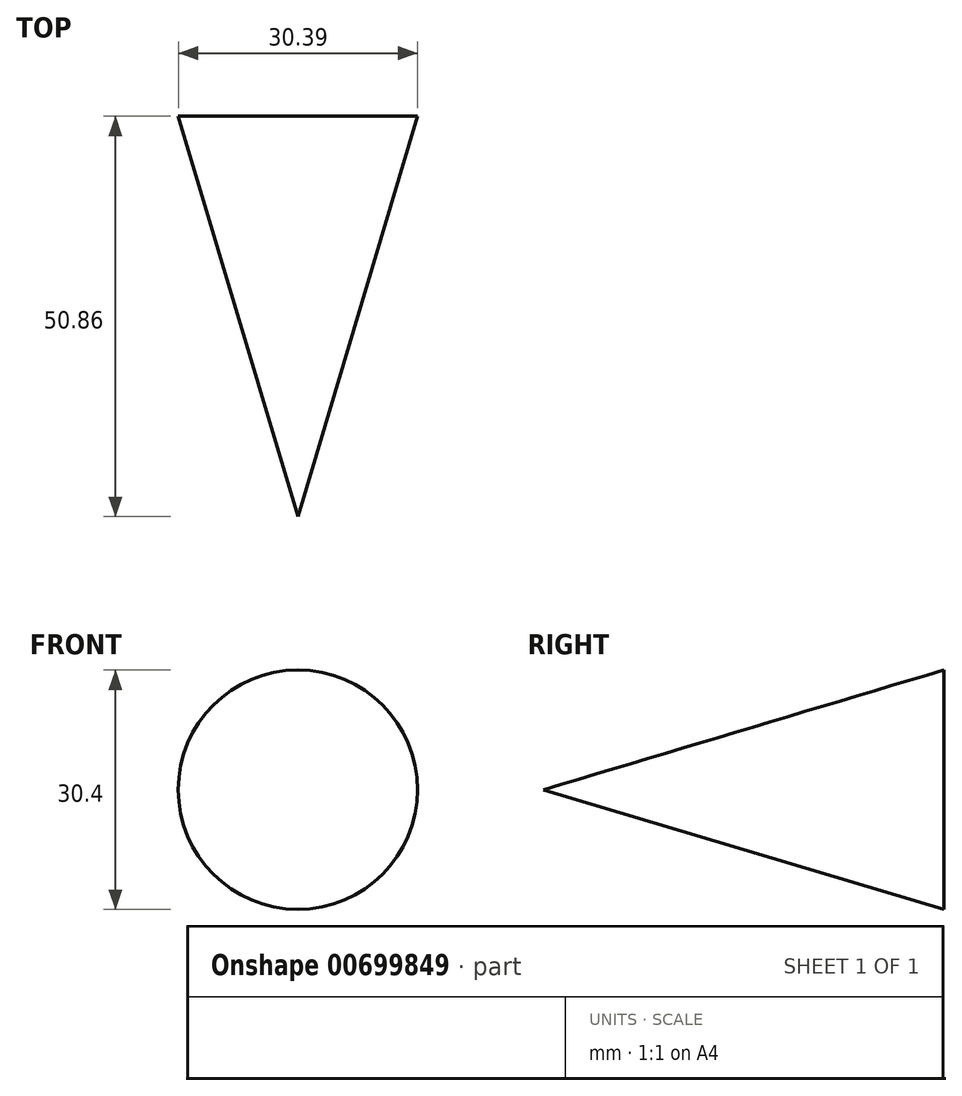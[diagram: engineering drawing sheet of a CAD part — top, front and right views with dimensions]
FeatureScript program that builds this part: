
annotation { "Feature Type Name" : "Feature", "Feature Type Description" : "" }
export const myFeature = defineFeature(function(context is Context, id is Id, definition is map)
    precondition{}
    {
        {
            var Q0;
            Q0=qCreatedBy(makeId("Top.planeOp"),FACE);
            var sketch = newSketch(context, id + "F0", { "sketchPlane" : qUnion([Q0])});
            skLineSegment(sketch, "E0", {"start": v(40.5, -9.77) * mm, "end": v(40.5, -60.63) * mm});
            skLineSegment(sketch, "E1", {"start": v(40.5, -60.63) * mm, "end": v(55.7, -9.77) * mm});
            skLineSegment(sketch, "E2", {"start": v(55.7, -9.77) * mm, "end": v(40.5, -9.77) * mm});
            skSolve(sketch);
        }
        {
            var Q0;
            Q0=makeQuery(id+"F0.imprint","IMPRINT",FACE,{"disambiguationData":[TD([[makeQuery(id+"F0.imprint","IMPRINT",EDGE,{"derivedFrom":sQuery(id+"F0.wireOp",EDGE,"E0")}),1.0]])]});
            var Q1;
            Q1=sQuery(id+"F0.wireOp",EDGE,"E0");
            revolve(context, id + "F1", {"entities" : qUnion([Q0]), "axis" : qUnion([Q1]), "revolveType" : RevolveType.FULL});
        }
    });
